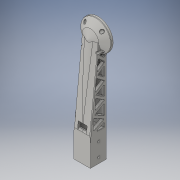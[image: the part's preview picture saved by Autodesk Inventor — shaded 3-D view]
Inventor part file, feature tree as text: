
AUTODESK INVENTOR PART (.ipt)
format: ipt  version: 2016 (Build 200138000, 138)  size: 1,543,680 bytes
history: native  units: in
note: dims shown in document units (in); Inventor stores cm internally (conversion verified against a paired STEP export)
features: sketch x16, fillet x12, extrude x11, chamfer x8, revolve x2, plane x1, loft x1, shell x1
ambient origin geometry x8: Origin, YZ Plane, XZ Plane, XY Plane, X Axis, Y Axis, Z Axis, Center Point
bodies: Solid1 (feature_tree)
feature tree (52):
  extrude  "Extrusion1"  Depth=1.5in
  plane  "Work Plane1"
  loft  "Loft1"
  revolve  "Revolution1"  [1 undecoded]
  sketch  "Sketch5"  dims[d18=0.75in]
  shell  "Shell1"  Thickness=0.75in
  extrude  "Extrusion2"  Depth=0.75in
  chamfer  "Chamfer1"  Angle=90.0deg  [1 undecoded]
  extrude  "Extrusion3"  TaperAngle=90.0deg  [1 undecoded]
  sketch  "Sketch9"  dims[d25=0.25in d26=1.25in]
  extrude  "Extrusion5"  Depth=1.25in
  revolve  "Revolution2"  [1 undecoded]
  extrude  "Extrusion6"  Depth=0.125in
  extrude  "Extrusion7"  Depth=0.125in
  chamfer  "Chamfer3"  Distance=0.125in
  chamfer  "Chamfer4"  Distance=0.125in
  extrude  "Extrusion8"  Depth=0.125in
  extrude  "Extrusion9"  Depth=0.125in
  chamfer  "Chamfer5"  Distance=0.125in
  chamfer  "Chamfer6"  Distance=0.125in
  extrude  "Extrusion10"  Depth=0.125in
  chamfer  "Chamfer7"  Distance=0.125in
  extrude  "Extrusion11"  Depth=0.125in
  extrude  "Extrusion12"  Depth=0.125in
  chamfer  "Chamfer8"  Distance=0.125in
  fillet  "Fillet1"  Radius=0.125in
  fillet  "Fillet2"  Radius=0.125in
  fillet  "Fillet3"  Radius=2.5in
  fillet  "Fillet4"  Radius=2.75in
  fillet  "Fillet7"  Radius=1.5in
  fillet  "Fillet8"  Radius=6.875in
  fillet  "Fillet9"  Radius=2.625in
  fillet  "Fillet10"  Radius=1.5in
  chamfer  "Chamfer9"  Distance=0.25in
  fillet  "Fillet11"  [1 undecoded]
  fillet  "Fillet12"  Radius=2.173in
  fillet  "Fillet13"  [1 undecoded]
  fillet  "Fillet14"  Radius=0.126in
  sketch  "Sketch1"  dims[d0=1.5in d1=1.5in]
  sketch  "Sketch2"  dims[d2=2.5in d3=0.0in d4=7.0in]
  sketch  "Sketch3"  dims[d12=135.0deg d14=0.75in d15=0.75in]
  sketch  "Sketch4"  dims[d16=1.5in d17=0.75in]
  sketch  "Sketch6"  dims[d19=22.5deg d20=0.0in d21=90.0deg]
  sketch  "Sketch8"  dims[d22=0.0in d23=90.0deg d24=90.0deg]
  sketch  "Sketch11"  dims[d27=1.25in d28=2.5313in d29=0.0in]
  sketch  "Sketch12"  dims[d30=0.1094in d31=0.125in d32=45.0deg d57=0.125in]
  sketch  "Sketch13"  dims[d58=0.125in d59=0.125in]
  sketch  "Sketch14"  dims[d60=0.125in]
  sketch  "Sketch15"  dims[d61=0.125in]
  sketch  "Sketch16"  dims[d62=0.125in]
  sketch  "Sketch17"  dims[d63=0.125in]
  sketch  "Sketch18"  dims[d64=0.125in d65=0.125in d66=0.125in d67=0.125in d68=0.125in d69=0.125in d70=0.125in d71=0.125in d72=0.125in d73=0.125in d74=0.125in d75=0.125in d76=0.125in d77=0.125in d78=2.5in d79=0.0in d93=2.75in d94=1.5in d95=6.875in d96=2.625in d97=1.5in d98=0.25in d99=0.0in d100=90.0deg d101=2.173in d102=45.0deg d103=0.126in d104=1.5748in d106=360.0deg d108=0.25in d109=0.0in d110=0.5in d111=0.75in d112=0.5in d113=0.25in d114=0.0in d115=0.25in d116=0.125in d117=45.0deg d118=0.5in d119=0.125in d120=45.0deg d121=1.5in d123=2.5in d124=1.1875in d125=0.1125in d126=0.0in d127=0.75in d128=0.5in d129=2.625in d130=0.1125in d131=0.0in d132=0.125in d133=0.125in d134=45.0deg d135=0.125in d136=0.125in d137=45.0deg d138=0.25in d139=1.5748in d141=360.0deg d143=1.25in d144=0.0in d145=0.0312in d146=0.125in d147=45.0deg d148=0.5in d149=1.25in d150=0.0in d151=0.0in d152=0.2188in d153=1.25in d154=0.0in d155=0.625in d156=0.125in d157=0.0in d158=0.125in d159=0.125in d160=45.0deg d161=0.25in d162=0.0625in d163=0.25in d164=0.25in d167=0.0625in d168=0.0625in d169=1.0in d170=0.0625in d171=0.0781in d172=0.125in d173=45.0deg d174=0.25in d175=0.0312in d176=0.0312in d177=0.0312in]
note: 6 required parameter values undecoded (feature->parameter linkage not recoverable at this tier; creation-order binding heuristic only, values carry confidence <= 0.55)